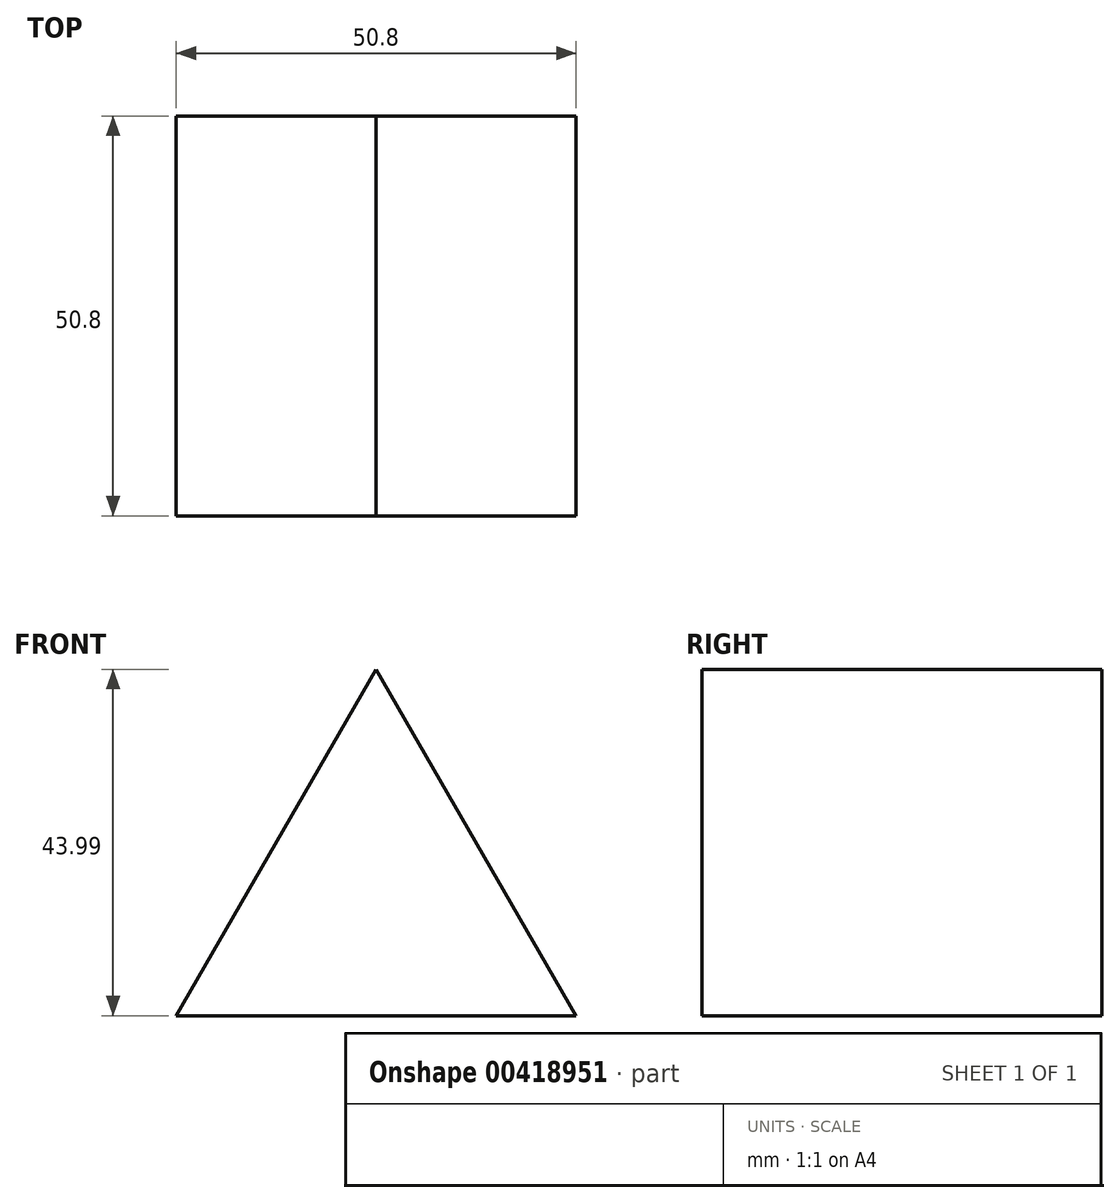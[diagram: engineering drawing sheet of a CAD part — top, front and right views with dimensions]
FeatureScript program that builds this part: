
annotation { "Feature Type Name" : "Feature", "Feature Type Description" : "" }
export const myFeature = defineFeature(function(context is Context, id is Id, definition is map)
    precondition{}
    {
        {
            var Q0;
            Q0=qCreatedBy(makeId("Front.planeOp"),FACE);
            var sketch = newSketch(context, id + "F0", { "sketchPlane" : qUnion([Q0])});
            skLineSegment(sketch, "E0", {"start": v(-50.8, 0) * mm, "end": v(0, 0) * mm});
            skLineSegment(sketch, "E1", {"start": v(-25.4, 44) * mm, "end": v(-50.8, 0) * mm});
            skLineSegment(sketch, "E2", {"start": v(-25.4, 44) * mm, "end": v(0, 0) * mm});
            skSolve(sketch);
        }
        {
            var Q0;
            Q0 = qSketchRegion(id + "F0", true);
            extrude(context, id + "F1", {"entities" : qUnion([Q0]), "depth" : 50.8 * mm});
        }
    });
